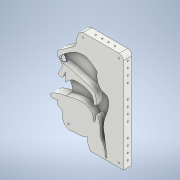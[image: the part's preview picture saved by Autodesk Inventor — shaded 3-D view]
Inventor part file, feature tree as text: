
AUTODESK INVENTOR PART (.ipt)
format: ipt  version: 2022.3 (Build 263350000, 350)  size: 500,736 bytes
history: mixed  units: in
note: dims shown in document units (in); Inventor stores cm internally (conversion verified against a paired STEP export)
features: sketch x7, hole x4, extrude x3, imported_body x1
ambient origin geometry x8: Origin, YZ Plane, XZ Plane, XY Plane, X Axis, Y Axis, Z Axis, Center Point
bodies: Solid1 (imported_parasolid), Body1 (imported_parasolid)
feature tree (15):
  extrude  "Extrusion1"  Depth=0.2087in
  extrude  "Extrusion2"  Depth=0.2087in TaperAngle=0.0deg
  hole  "Hole1"  [1 undecoded]
  extrude  "Extrusion3"  Depth=0.5906in
  hole  "Hole2"  [1 undecoded]
  hole  "Hole3"  [1 undecoded]
  hole  "Hole4"  [1 undecoded]
  sketch  "Sketch1"  dims[d0=0.2087in d1=0.0in d2=1.2598in]
  sketch  "Sketch2"  dims[d3=1.2598in d4=0.2087in d5=0.0in]
  sketch  "Sketch3"  dims[d6=0.2953in d7=0.5906in]
  sketch  "Sketch4"  dims[d8=0.2953in d9=0.5906in]
  sketch  "Sketch5"  dims[d10=0.0866in d11=0.2362in d12=0.122in d13=0.1614in d14=90.0deg d15=0.0472in d16=0.0in d17=0.2756in]
  sketch  "Sketch6"  dims[d18=0.2087in d19=0.0in d20=0.3937in]
  sketch  "Sketch7"  dims[d21=0.0866in d22=0.2362in d23=0.122in d24=0.1614in d25=90.0deg d26=0.0472in d27=0.0in d28=0.2756in d29=0.3937in d30=0.2953in d31=0.5906in d32=0.2953in d33=0.5906in d38=0.5906in d39=0.5906in d40=0.5906in d41=0.5906in d42=0.5906in d43=0.5906in d44=0.5906in d45=0.5906in d46=0.0866in d47=0.2362in d48=0.122in d49=0.1614in d50=90.0deg d51=0.0472in d52=0.0in d53=0.2953in d54=0.5906in d55=0.2953in d56=0.5906in d57=0.0866in d58=0.2362in d59=0.122in d60=0.1614in d61=90.0deg d62=0.0472in d63=0.0in]
  imported_body  NMx_Import_Brep_tag  [imported B-rep: ~14 faces, bbox_mm=[32.65, 5.3, 0.0]]
note: 4 required parameter values undecoded (feature->parameter linkage not recoverable at this tier; creation-order binding heuristic only, values carry confidence <= 0.55)
